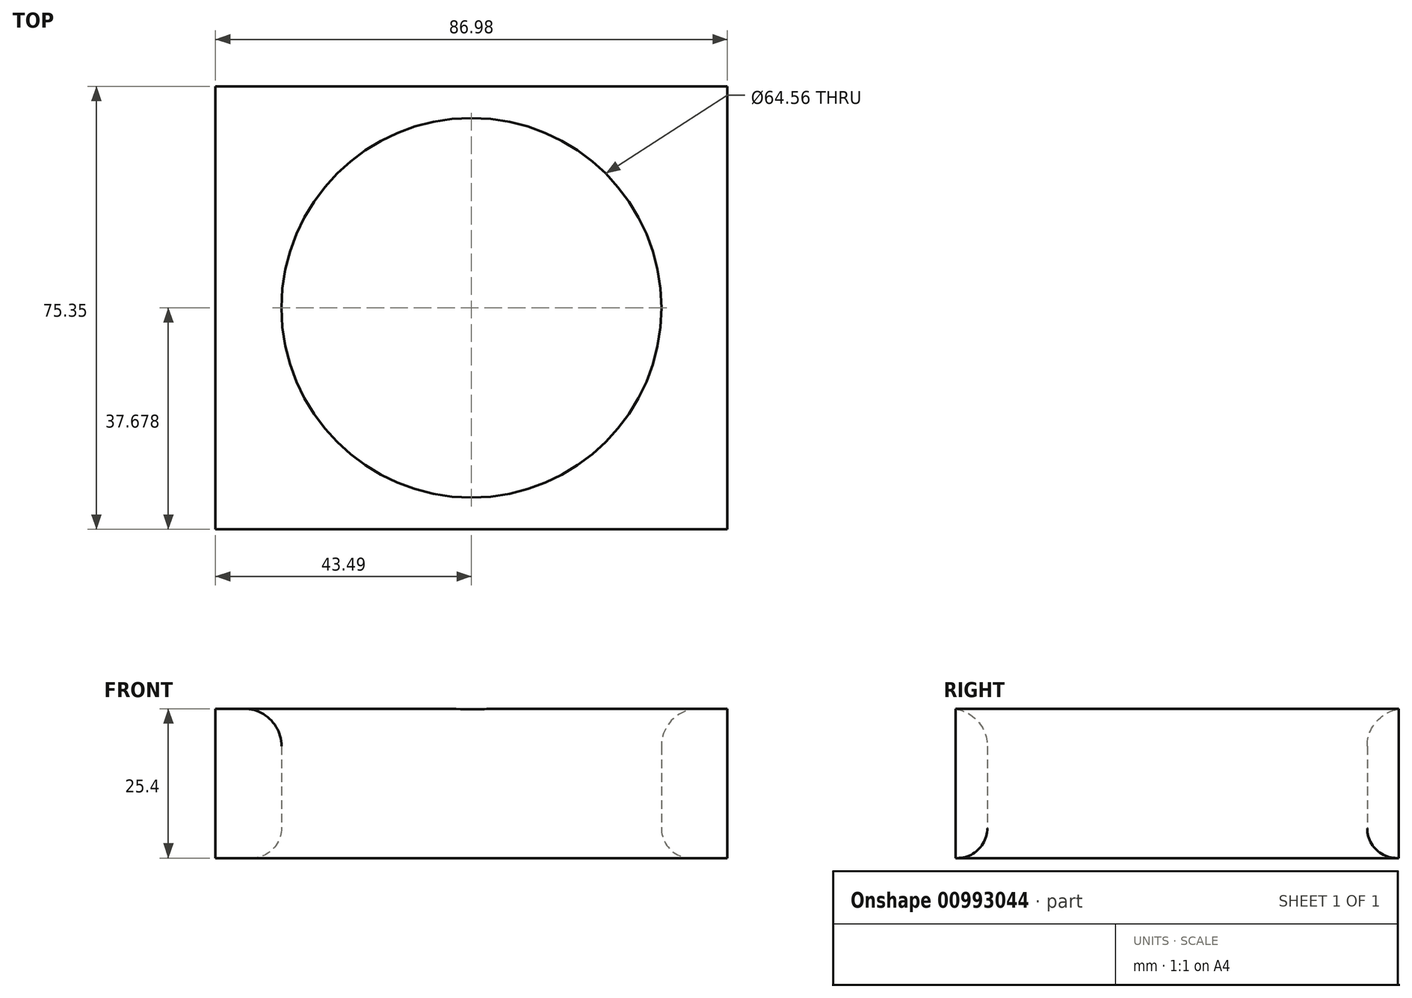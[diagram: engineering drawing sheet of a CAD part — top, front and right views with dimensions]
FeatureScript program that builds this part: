
annotation { "Feature Type Name" : "Feature", "Feature Type Description" : "" }
export const myFeature = defineFeature(function(context is Context, id is Id, definition is map)
    precondition{}
    {
        {
            var Q0;
            Q0=qCreatedBy(makeId("Top.planeOp"),FACE);
            var sketch = newSketch(context, id + "F0", { "sketchPlane" : qUnion([Q0])});
            skLineSegment(sketch, "E0.bottom", {"start": v(-30.4, 31.74) * mm, "end": v(56.58, 31.74) * mm});
            skLineSegment(sketch, "E0.top", {"start": v(-30.4, -43.6) * mm, "end": v(56.58, -43.6) * mm});
            skLineSegment(sketch, "E0.left", {"start": v(-30.4, 31.74) * mm, "end": v(-30.4, -43.6) * mm});
            skLineSegment(sketch, "E0.right", {"start": v(56.58, 31.74) * mm, "end": v(56.58, -43.6) * mm});
            skCircle(sketch, "E1", {"center": v(13.09, -5.93) * mm, "radius": 32.28 * mm});
            skPoint(sketch, "E1.centerSnap0", {"position": v(-30.4, -5.93) * mm});
            skPoint(sketch, "E1.centerSnap1", {"position": v(13.09, 31.74) * mm});
            skSolve(sketch);
        }
        {
            var Q0;
            Q0=makeQuery(id+"F0.imprint","IMPRINT",FACE,{"disambiguationData":[TD([[makeQuery(id+"F0.imprint","IMPRINT",EDGE,{"derivedFrom":sQuery(id+"F0.wireOp",EDGE,"E0.bottom")}),-1.0]])]});
            extrude(context, id + "F1", {"entities" : qUnion([Q0]), "depth" : 25.4 * mm, "offsetDistance" : 25.4 * mm});
        }
        {
            var Q0;
            Q0=makeQuery(id+"F1.opExtrude","CAP_EDGE",EDGE,{"disambiguationData":[OSD([sQuery(id+"F0.wireOp",EDGE,"E1")])],"isStart":false});
            fillet(context, id + "F2", {"entities" : qUnion([Q0]), "radius" : 6.35 * mm, "tangentPropagation" : true, "allowEdgeOverflow" : false});
        }
        {
            var Q0;
            Q0=makeQuery(id+"F1.opExtrude","CAP_EDGE",EDGE,{"disambiguationData":[OSD([sQuery(id+"F0.wireOp",EDGE,"E1")])],"isStart":true});
            fillet(context, id + "F3", {"entities" : qUnion([Q0]), "radius" : 5.08 * mm, "tangentPropagation" : true, "allowEdgeOverflow" : false});
        }
    });
